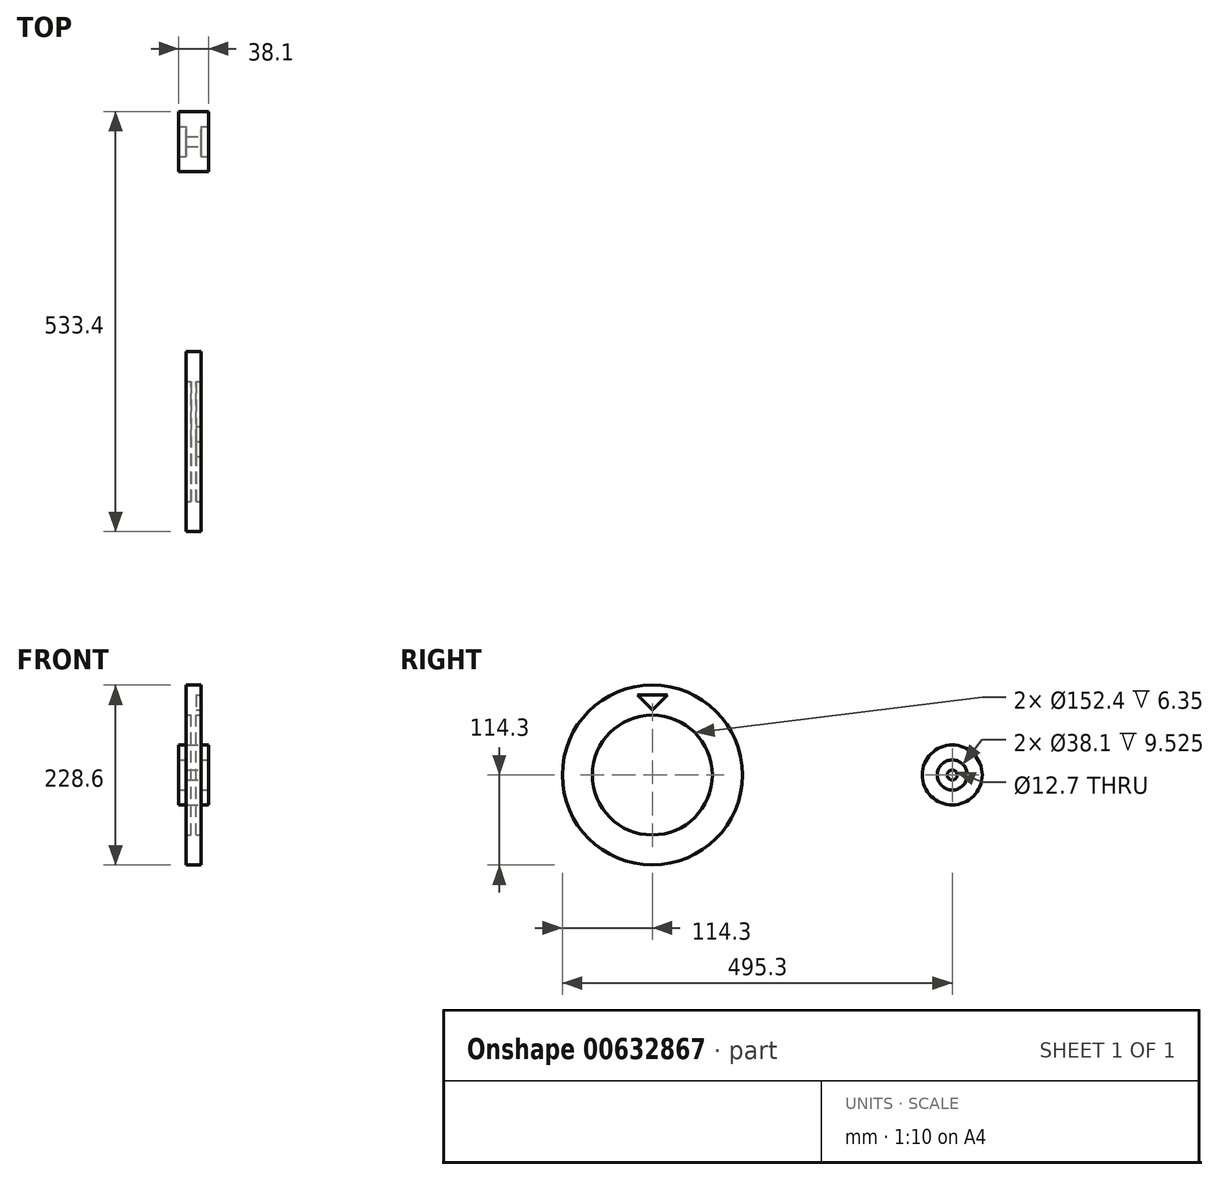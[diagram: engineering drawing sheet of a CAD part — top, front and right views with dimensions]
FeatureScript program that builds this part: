
annotation { "Feature Type Name" : "Feature", "Feature Type Description" : "" }
export const myFeature = defineFeature(function(context is Context, id is Id, definition is map)
    precondition{}
    {
        {
            var Q0;
            Q0=qCreatedBy(makeId("Front.planeOp"),FACE);
            var sketch = newSketch(context, id + "F0", { "sketchPlane" : qUnion([Q0])});
            skLineSegment(sketch, "E0", {"start": v(-9.53, 19.05) * mm, "end": v(-9.53, -19.05) * mm});
            skLineSegment(sketch, "E1", {"start": v(-9.53, -19.05) * mm, "end": v(-19.05, -19.05) * mm});
            skLineSegment(sketch, "E2", {"start": v(-19.05, -19.05) * mm, "end": v(-19.05, -38.1) * mm});
            skLineSegment(sketch, "E3", {"start": v(-19.05, -38.1) * mm, "end": v(19.05, -38.1) * mm});
            skLineSegment(sketch, "E4", {"start": v(19.05, -38.1) * mm, "end": v(19.05, -19.05) * mm});
            skLineSegment(sketch, "E5", {"start": v(19.05, -19.05) * mm, "end": v(9.52, -19.05) * mm});
            skLineSegment(sketch, "E6", {"start": v(9.53, -19.05) * mm, "end": v(9.53, 19.05) * mm});
            skLineSegment(sketch, "E7", {"start": v(9.53, 19.05) * mm, "end": v(19.05, 19.05) * mm});
            skLineSegment(sketch, "E8", {"start": v(19.05, 19.05) * mm, "end": v(19.05, 38.1) * mm});
            skLineSegment(sketch, "E9", {"start": v(19.05, 38.1) * mm, "end": v(-19.05, 38.1) * mm});
            skLineSegment(sketch, "E10", {"start": v(-19.05, 38.1) * mm, "end": v(-19.05, 19.05) * mm});
            skLineSegment(sketch, "E11", {"start": v(-19.05, 19.05) * mm, "end": v(-9.53, 19.05) * mm});
            skPoint(sketch, "E12", {"position": v(0, 38.1) * mm});
            skPoint(sketch, "E13", {"position": v(0, -38.1) * mm});
            skLineSegment(sketch, "E14", {"start": v(0, -38.1) * mm, "end": v(0, 38.1) * mm});
            skPoint(sketch, "E15", {"position": v(0, 0) * mm});
            skPoint(sketch, "E16", {"position": v(-9.53, 0) * mm});
            skPoint(sketch, "E17", {"position": v(9.53, 0) * mm});
            skLineSegment(sketch, "E18", {"start": v(9.53, 0) * mm, "end": v(-9.53, 0) * mm});
            skLineSegment(sketch, "E19.bottom", {"start": v(9.53, 6.35) * mm, "end": v(-9.53, 6.35) * mm});
            skLineSegment(sketch, "E19.top", {"start": v(9.53, -6.35) * mm, "end": v(-9.53, -6.35) * mm});
            skLineSegment(sketch, "E19.left", {"start": v(9.53, 6.35) * mm, "end": v(9.53, -6.35) * mm});
            skLineSegment(sketch, "E19.right", {"start": v(-9.53, 6.35) * mm, "end": v(-9.53, -6.35) * mm});
            skLineSegment(sketch, "E20", {"start": v(9.53, -19.05) * mm, "end": v(-9.53, -19.05) * mm});
            skSolve(sketch);
        }
        {
            var Q0;
            {var subQ0=sQuery(id+"F0.wireOp",EDGE,"E10");Q0=makeQuery(id+"F0.imprint","IMPRINT",FACE,{"disambiguationData":[TD([[makeQuery(id+"F0.imprint","IMPRINT",EDGE,{"derivedFrom":subQ0}),1.0]])]});}
            var Q1;
            {var subQ8=sQuery(id+"F0.wireOp",EDGE,"E7");Q1=makeQuery(id+"F0.imprint","IMPRINT",FACE,{"disambiguationData":[TD([[makeQuery(id+"F0.imprint","IMPRINT",EDGE,{"derivedFrom":subQ8}),1.0]])]});}
            var Q2;
            Q2=sQuery(id+"F0.wireOp",EDGE,"E18");
            revolve(context, id + "F1", {"entities" : qUnion([Q0, Q1]), "axis" : qUnion([Q2]), "revolveType" : RevolveType.FULL});
        }
        {
            var Q0;
            Q0=qCreatedBy(makeId("Front.planeOp"),FACE);
            cPlane(context, id + "F2", {"entities" : qUnion([Q0]), "cplaneType" : CPlaneType.OFFSET, "offset" : 381 * mm, "width" : 152.4 * mm, "height" : 152.4 * mm});
        }
        {
            var Q0;
            Q0=qCreatedBy(id+"F2.planeOp",FACE);
            var sketch = newSketch(context, id + "F3", { "sketchPlane" : qUnion([Q0])});
            skLineSegment(sketch, "E21", {"start": v(3.17, 0) * mm, "end": v(-3.18, 0) * mm});
            skLineSegment(sketch, "E22", {"start": v(3.17, 0) * mm, "end": v(3.17, 76.2) * mm});
            skLineSegment(sketch, "E23", {"start": v(3.17, 76.2) * mm, "end": v(-9.53, 76.2) * mm});
            skLineSegment(sketch, "E24", {"start": v(-9.53, 76.2) * mm, "end": v(-9.53, 114.3) * mm});
            skLineSegment(sketch, "E25", {"start": v(-9.53, 114.3) * mm, "end": v(9.52, 114.3) * mm});
            skLineSegment(sketch, "E26", {"start": v(9.52, 114.3) * mm, "end": v(9.52, 76.2) * mm});
            skLineSegment(sketch, "E27", {"start": v(9.52, 76.2) * mm, "end": v(-3.17, 76.2) * mm});
            skLineSegment(sketch, "E28", {"start": v(-3.18, 76.2) * mm, "end": v(-3.17, 0) * mm});
            skLineSegment(sketch, "E29.MirrorCS", {"start": v(-9.52, -114.3) * mm, "end": v(9.53, -114.3) * mm});
            skLineSegment(sketch, "E30.MirrorCS", {"start": v(9.53, -76.2) * mm, "end": v(-3.17, -76.2) * mm});
            skLineSegment(sketch, "E31.MirrorCS", {"start": v(-3.17, -76.2) * mm, "end": v(-3.18, 0) * mm});
            skLineSegment(sketch, "E32.MirrorCS", {"start": v(9.53, -114.3) * mm, "end": v(9.53, -76.2) * mm});
            skLineSegment(sketch, "E33.MirrorCS", {"start": v(3.17, 0) * mm, "end": v(3.17, -76.2) * mm});
            skLineSegment(sketch, "E34.MirrorCS", {"start": v(3.18, -76.2) * mm, "end": v(-9.52, -76.2) * mm});
            skLineSegment(sketch, "E35.MirrorCS", {"start": v(-9.52, -76.2) * mm, "end": v(-9.52, -114.3) * mm});
            skLineSegment(sketch, "E36.bottom", {"start": v(3.17, 12.7) * mm, "end": v(-3.17, 12.7) * mm});
            skLineSegment(sketch, "E36.top", {"start": v(3.17, -12.7) * mm, "end": v(-3.17, -12.7) * mm});
            skLineSegment(sketch, "E36.left", {"start": v(-3.17, 12.7) * mm, "end": v(-3.17, -12.7) * mm});
            skLineSegment(sketch, "E36.right", {"start": v(3.17, 12.7) * mm, "end": v(3.17, -12.7) * mm});
            skPoint(sketch, "E36.middle", {"position": v(0, 0) * mm});
            skLineSegment(sketch, "E37", {"start": v(-3.18, 76.2) * mm, "end": v(3.17, 76.2) * mm});
            skLineSegment(sketch, "E38", {"start": v(3.18, -76.2) * mm, "end": v(-3.17, -76.2) * mm});
            skSolve(sketch);
        }
        {
            var Q0;
            Q0=makeQuery(id+"F3.imprint","IMPRINT",FACE,{"disambiguationData":[TD([[makeQuery(id+"F3.imprint","IMPRINT",EDGE,{"derivedFrom":sQuery(id+"F3.wireOp",EDGE,"E22")}),1.0]])]});
            var Q1;
            Q1=makeQuery(id+"F3.imprint","IMPRINT",FACE,{"disambiguationData":[TD([[makeQuery(id+"F3.imprint","IMPRINT",EDGE,{"derivedFrom":sQuery(id+"F3.wireOp",EDGE,"E23")}),-1.0]])]});
            var Q2;
            Q2=sQuery(id+"F3.wireOp",EDGE,"E21");
            revolve(context, id + "F4", {"entities" : qUnion([Q0, Q1]), "axis" : qUnion([Q2]), "revolveType" : RevolveType.FULL});
        }
        {
            var Q0;
            Q0=makeQuery(id+"F4.opRevolve","SWEPT_FACE",FACE,{"disambiguationData":[OSD([sQuery(id+"F3.wireOp",EDGE,"E26")])]});
            var sketch = newSketch(context, id + "F5", { "sketchPlane" : qUnion([Q0])});
            skLineSegment(sketch, "E39", {"start": v(-400.08, 101.6) * mm, "end": v(-381.03, 82.55) * mm});
            skLineSegment(sketch, "E40", {"start": v(-381.03, 82.55) * mm, "end": v(-361.98, 101.6) * mm});
            skLineSegment(sketch, "E41", {"start": v(-361.98, 101.6) * mm, "end": v(-400.08, 101.6) * mm});
            skPoint(sketch, "E42", {"position": v(-381.03, 101.6) * mm});
            skLineSegment(sketch, "E43", {"start": v(-381.03, 101.6) * mm, "end": v(-381.03, 82.55) * mm});
            skSolve(sketch);
        }
        {
            var Q0;
            {var subQ0=sQuery(id+"F5.wireOp",EDGE,"E39");Q0=makeQuery(id+"F5.imprint","IMPRINT",FACE,{"disambiguationData":[TD([[makeQuery(id+"F5.imprint","IMPRINT",EDGE,{"derivedFrom":subQ0}),1.0]])]});}
            var Q1;
            {var subQ0=sQuery(id+"F5.wireOp",EDGE,"E40");Q1=makeQuery(id+"F5.imprint","IMPRINT",FACE,{"disambiguationData":[TD([[makeQuery(id+"F5.imprint","IMPRINT",EDGE,{"derivedFrom":subQ0}),1.0]])]});}
            extrude(context, id + "F6", {"entities" : qUnion([Q0, Q1]), "operationType" : NewBodyOperationType.REMOVE, "oppositeDirection" : true, "depth" : 6.35 * mm, "offsetDistance" : 25.4 * mm});
        }
    });
